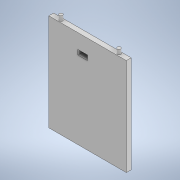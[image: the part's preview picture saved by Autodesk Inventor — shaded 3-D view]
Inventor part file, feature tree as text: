
AUTODESK INVENTOR PART (.ipt)
format: ipt  version: 2020 (Build 240168000, 168)  size: 119,296 bytes
history: native  units: mm
features: extrude x4, sketch x4
ambient origin geometry x8: Origin, YZ Plane, XZ Plane, XY Plane, X Axis, Y Axis, Z Axis, Center Point
bodies: Solid1 (feature_tree)
feature tree (8):
  extrude  "Extrusion1"  Depth=5.0mm
  extrude  "Extrusion2"  Depth=10.0mm
  extrude  "Extrusion3"  Depth=3.5mm
  extrude  "Extrusion4"  Depth=10.0mm
  sketch  "Sketch1"  dims[d0=80.0mm d1=5.0mm]
  sketch  "Sketch2"  dims[d2=100.0mm d3=0.0mm d4=10.0mm]
  sketch  "Sketch3"  dims[d5=2.5mm d6=3.5mm]
  sketch  "Sketch4"  dims[d7=5.0mm d8=0.0mm d9=10.0mm d10=2.5mm d11=3.5mm d12=5.0mm d13=0.0mm d14=40.0mm d15=80.0mm d16=10.0mm d17=5.0mm d18=10.0mm d19=0.0mm]
